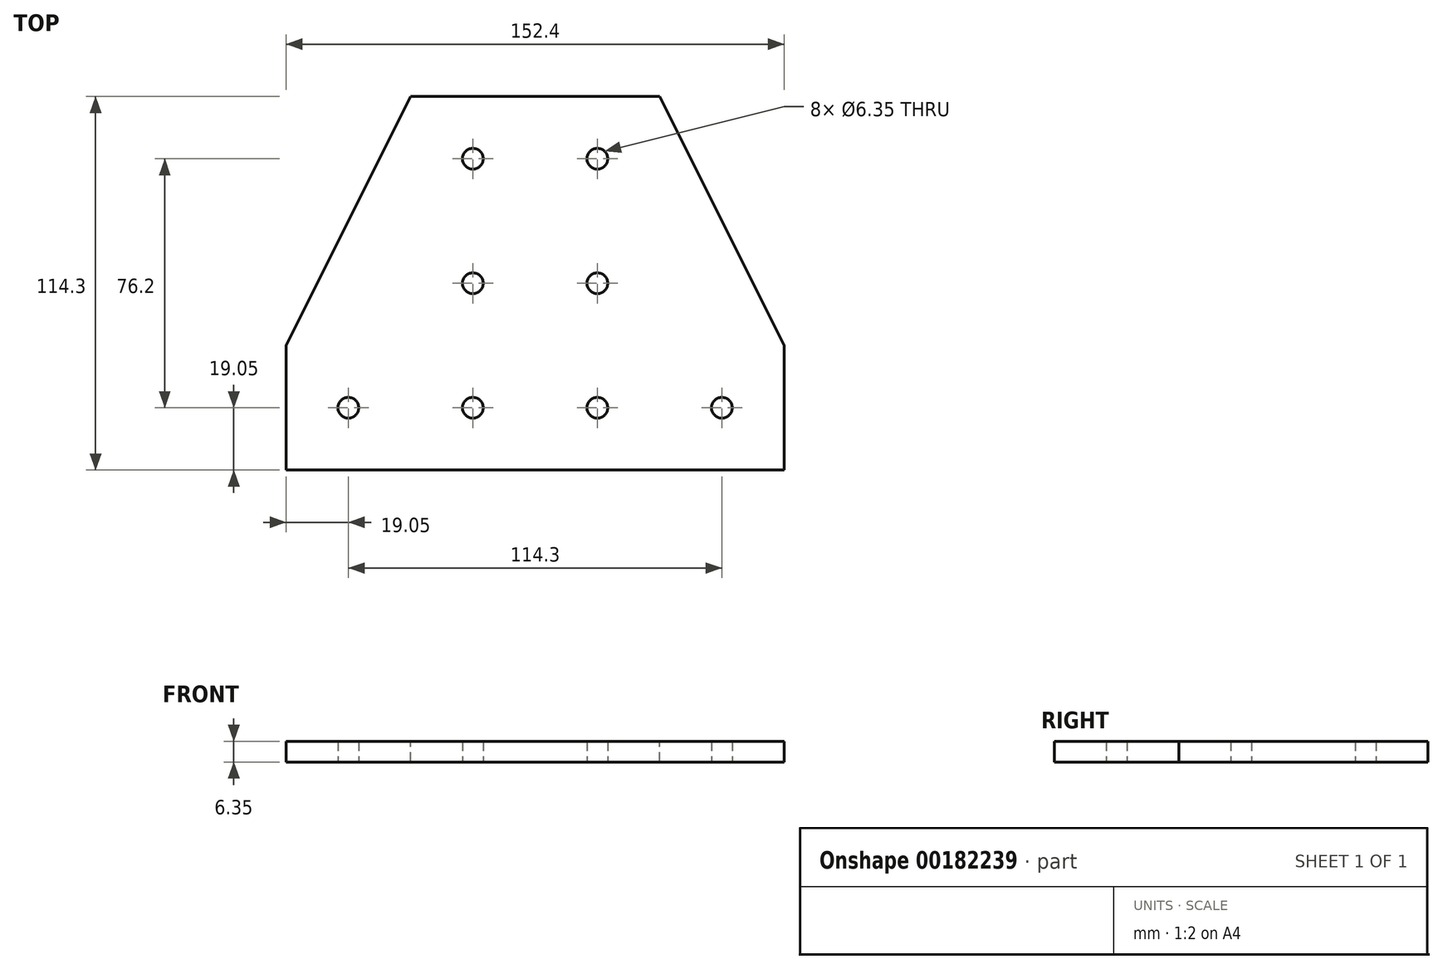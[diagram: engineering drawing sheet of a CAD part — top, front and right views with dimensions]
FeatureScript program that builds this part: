
annotation { "Feature Type Name" : "Feature", "Feature Type Description" : "" }
export const myFeature = defineFeature(function(context is Context, id is Id, definition is map)
    precondition{}
    {
        {
            var Q0;
            Q0=qCreatedBy(makeId("Top.planeOp"),FACE);
            var sketch = newSketch(context, id + "F0", { "sketchPlane" : qUnion([Q0])});
            skLineSegment(sketch, "E0", {"start": v(0, 0) * mm, "end": v(0, 38.1) * mm});
            skLineSegment(sketch, "E1", {"start": v(0, 38.1) * mm, "end": v(38.1, 114.3) * mm});
            skLineSegment(sketch, "E2", {"start": v(38.1, 114.3) * mm, "end": v(114.3, 114.3) * mm});
            skLineSegment(sketch, "E3", {"start": v(114.3, 114.3) * mm, "end": v(152.4, 38.1) * mm});
            skLineSegment(sketch, "E4", {"start": v(152.4, 38.1) * mm, "end": v(152.4, 0) * mm});
            skLineSegment(sketch, "E5", {"start": v(152.4, 0) * mm, "end": v(0, 0) * mm});
            skPoint(sketch, "E6", {"position": v(19.05, 19.05) * mm});
            skPoint(sketch, "E7", {"position": v(57.15, 19.05) * mm});
            skPoint(sketch, "E8", {"position": v(95.25, 19.05) * mm});
            skPoint(sketch, "E9", {"position": v(133.35, 19.05) * mm});
            skPoint(sketch, "E10", {"position": v(57.15, 95.25) * mm});
            skPoint(sketch, "E11", {"position": v(95.25, 95.25) * mm});
            skPoint(sketch, "E12", {"position": v(57.15, 57.15) * mm});
            skPoint(sketch, "E13", {"position": v(95.25, 57.15) * mm});
            skSolve(sketch);
        }
        {
            var Q0;
            Q0=qSketchRegion(id+"F0",true);
            extrude(context, id + "F1", {"entities" : qUnion([Q0]), "oppositeDirection" : true, "depth" : 6.35 * mm});
        }
        {
            var Q0;
            Q0=sQuery(id+"F0.wireOp",VERTEX,"E10");
            var Q1;
            Q1=sQuery(id+"F0.wireOp",VERTEX,"E11");
            var Q2;
            Q2=sQuery(id+"F0.wireOp",VERTEX,"E13");
            var Q3;
            Q3=sQuery(id+"F0.wireOp",VERTEX,"E12");
            var Q4;
            Q4=sQuery(id+"F0.wireOp",VERTEX,"E6");
            var Q5;
            Q5=sQuery(id+"F0.wireOp",VERTEX,"E7");
            var Q6;
            Q6=sQuery(id+"F0.wireOp",VERTEX,"E8");
            var Q7;
            Q7=sQuery(id+"F0.wireOp",VERTEX,"E9");
            var Q8;
            Q8=makeQuery(id+"F1.opExtrude","SWEPT_BODY",BODY,{"disambiguationData":[OSD([sQuery(id+"F0.wireOp",EDGE,"E0"),sQuery(id+"F0.wireOp",EDGE,"E1"),sQuery(id+"F0.wireOp",EDGE,"E2"),sQuery(id+"F0.wireOp",EDGE,"E3"),sQuery(id+"F0.wireOp",EDGE,"E4"),sQuery(id+"F0.wireOp",EDGE,"E5")])]});
            hole(context, id + "F2", {"style" : HoleStyle.SIMPLE, "holeDiameter" : 6.35 * mm, "endStyle" : HoleEndStyle.THROUGH, "locations" : qUnion([Q0, Q1, Q2, Q3, Q4, Q5, Q6, Q7]), "scope" : qUnion([Q8])});
        }
    });
